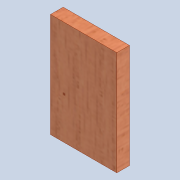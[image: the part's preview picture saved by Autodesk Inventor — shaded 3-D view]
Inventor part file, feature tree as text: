
AUTODESK INVENTOR PART (.ipt)
format: ipt  version: 2020 (Build 240168000, 168)  size: 208,384 bytes
history: native  units: mm
features: extrude x1, sketch x1
ambient origin geometry x8: Origin, YZ Plane, XZ Plane, XY Plane, X Axis, Y Axis, Z Axis, Center Point
bodies: Solid1 (feature_tree)
feature tree (2):
  extrude  "Extrusion1"  Depth=66.0mm
  sketch  "Sketch1"  dims[d0=42.0mm d1=66.0mm d2=8.0mm d3=0.0mm]
